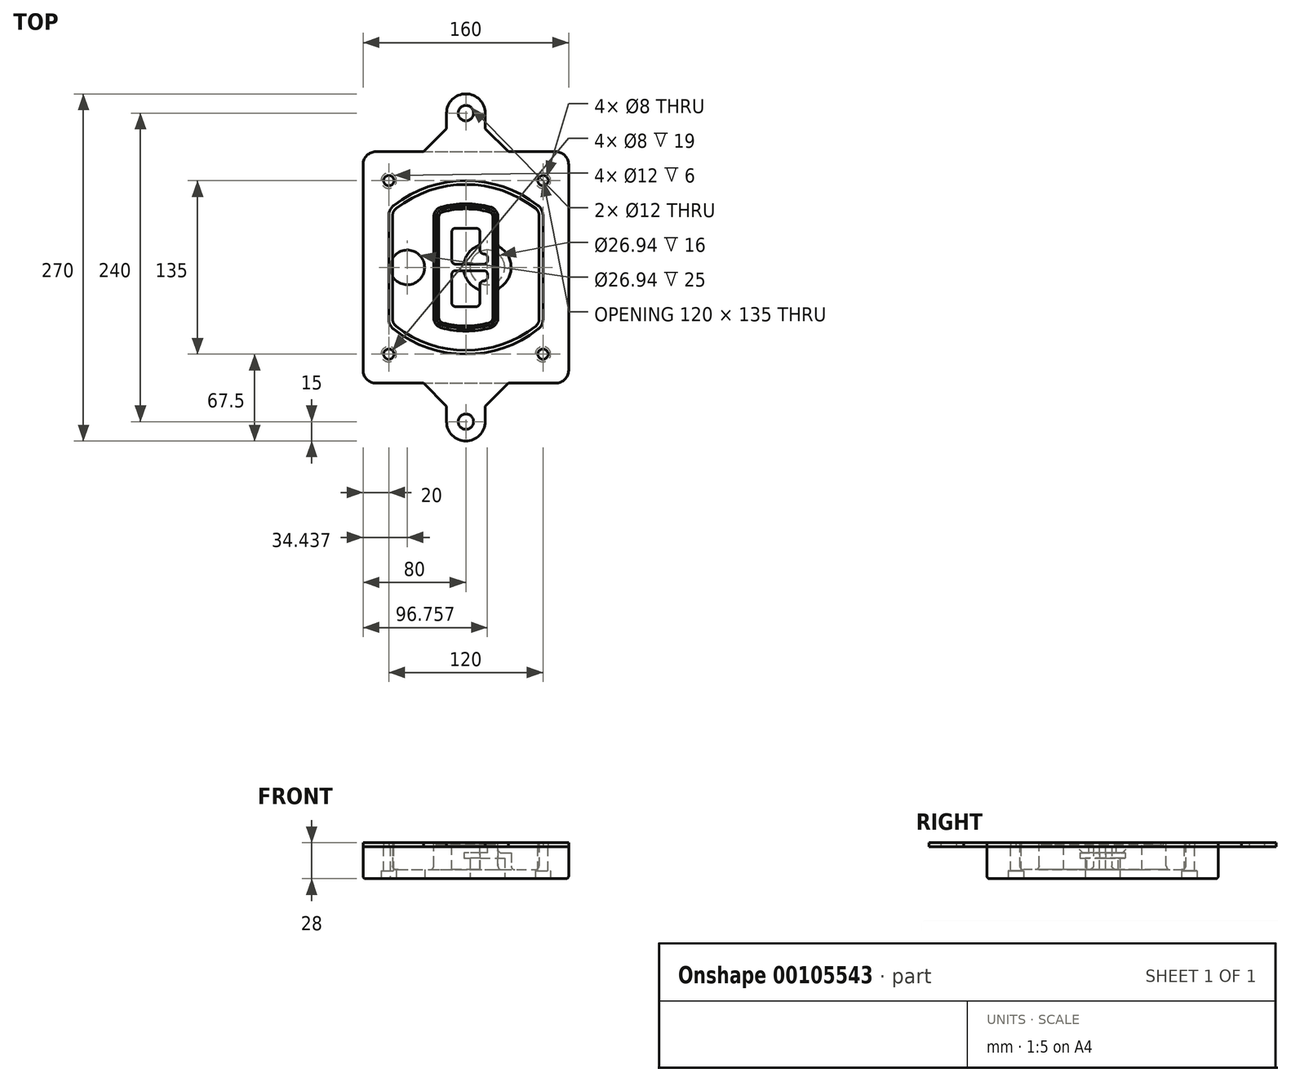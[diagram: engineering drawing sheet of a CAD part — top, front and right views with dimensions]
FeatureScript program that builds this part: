
annotation { "Feature Type Name" : "Feature", "Feature Type Description" : "" }
export const myFeature = defineFeature(function(context is Context, id is Id, definition is map)
    precondition{}
    {
        {
            var Q0;
            Q0=qCreatedBy(makeId("Top.planeOp"),FACE);
            var sketch = newSketch(context, id + "F0", { "sketchPlane" : qUnion([Q0])});
            skPoint(sketch, "E0.rect.middle", {"position": v(0, 0) * mm});
            skLineSegment(sketch, "E1.bottom", {"start": v(-70, -90) * mm, "end": v(70, -90) * mm});
            skLineSegment(sketch, "E1.top", {"start": v(-70, 90) * mm, "end": v(70, 90) * mm});
            skLineSegment(sketch, "E1.left", {"start": v(-80, -80) * mm, "end": v(-80, 80) * mm});
            skLineSegment(sketch, "E1.right", {"start": v(80, -80) * mm, "end": v(80, 80) * mm});
            skLineSegment(sketch, "E2", {"start": v(-80, 90) * mm, "end": v(80, -90) * mm, "construction": true});
            skLineSegment(sketch, "E3", {"start": v(80, 90) * mm, "end": v(-80, -90) * mm, "construction": true});
            skCircle(sketch, "E4", {"center": v(-60, 67.5) * mm, "radius": 4 * mm});
            skCircle(sketch, "E5", {"center": v(60, 67.5) * mm, "radius": 4 * mm});
            skCircle(sketch, "E6", {"center": v(60, -67.5) * mm, "radius": 4 * mm});
            skCircle(sketch, "E7", {"center": v(-60, -67.5) * mm, "radius": 4 * mm});
            skLineSegment(sketch, "E8", {"start": v(-60, 67.5) * mm, "end": v(60, 67.5) * mm, "construction": true});
            skLineSegment(sketch, "E9", {"start": v(60, 67.5) * mm, "end": v(60, -67.5) * mm, "construction": true});
            skLineSegment(sketch, "E10", {"start": v(60, -67.5) * mm, "end": v(-60, -67.5) * mm, "construction": true});
            skLineSegment(sketch, "E11", {"start": v(-60, -67.5) * mm, "end": v(-60, 67.5) * mm, "construction": true});
            skLineSegment(sketch, "E12", {"start": v(-60, 40.3) * mm, "end": v(-60, -40.3) * mm});
            skLineSegment(sketch, "E13", {"start": v(60, 40.3) * mm, "end": v(60, -40.3) * mm});
            skArc(sketch, "E14", {"start": v(56.15, 48.18) * mm, "mid": v(0, 67.5) * mm, "end": v(-56.15, 48.18) * mm});
            skArc(sketch, "E15", {"start": v(-56.15, -48.18) * mm, "mid": v(0, -67.5) * mm, "end": v(56.15, -48.18) * mm});
            skLineSegment(sketch, "E16", {"start": v(-60, 0) * mm, "end": v(60, 0) * mm, "construction": true});
            skPoint(sketch, "E17.visualSharp", {"position": v(-60, -45) * mm});
            skArc(sketch, "E17.filletArc", {"start": v(-60, -40.3) * mm, "mid": v(-58.99, -44.68) * mm, "end": v(-56.15, -48.18) * mm});
            skPoint(sketch, "E18.visualSharp", {"position": v(-60, 45) * mm});
            skArc(sketch, "E18.filletArc", {"start": v(-56.15, 48.18) * mm, "mid": v(-58.99, 44.68) * mm, "end": v(-60, 40.3) * mm});
            skPoint(sketch, "E19.visualSharp", {"position": v(60, 45) * mm});
            skArc(sketch, "E19.filletArc", {"start": v(60, 40.3) * mm, "mid": v(58.99, 44.68) * mm, "end": v(56.15, 48.18) * mm});
            skPoint(sketch, "E20.visualSharp", {"position": v(60, -45) * mm});
            skArc(sketch, "E20.filletArc", {"start": v(56.15, -48.18) * mm, "mid": v(58.99, -44.68) * mm, "end": v(60, -40.3) * mm});
            skPoint(sketch, "E21.visualSharp", {"position": v(-80, 90) * mm});
            skArc(sketch, "E21.filletArc", {"start": v(-70, 90) * mm, "mid": v(-77.07, 87.07) * mm, "end": v(-80, 80) * mm});
            skPoint(sketch, "E22.visualSharp", {"position": v(80, 90) * mm});
            skArc(sketch, "E22.filletArc", {"start": v(80, 80) * mm, "mid": v(77.07, 87.07) * mm, "end": v(70, 90) * mm});
            skPoint(sketch, "E23.visualSharp", {"position": v(80, -90) * mm});
            skArc(sketch, "E23.filletArc", {"start": v(70, -90) * mm, "mid": v(77.07, -87.07) * mm, "end": v(80, -80) * mm});
            skPoint(sketch, "E24.visualSharp", {"position": v(-80, -90) * mm});
            skArc(sketch, "E24.filletArc", {"start": v(-80, -80) * mm, "mid": v(-77.07, -87.07) * mm, "end": v(-70, -90) * mm});
            skArc(sketch, "E25.0", {"start": v(57, 40.3) * mm, "mid": v(56.3, 43.36) * mm, "end": v(54.3, 45.81) * mm});
            skLineSegment(sketch, "E25.1", {"start": v(57, 40.3) * mm, "end": v(57, -40.3) * mm});
            skArc(sketch, "E25.2", {"start": v(54.3, -45.81) * mm, "mid": v(56.3, -43.36) * mm, "end": v(57, -40.3) * mm});
            skArc(sketch, "E25.3", {"start": v(-54.3, -45.81) * mm, "mid": v(0, -64.5) * mm, "end": v(54.3, -45.81) * mm});
            skArc(sketch, "E25.4", {"start": v(-57, -40.3) * mm, "mid": v(-56.3, -43.36) * mm, "end": v(-54.3, -45.81) * mm});
            skArc(sketch, "E25.5", {"start": v(54.3, 45.81) * mm, "mid": v(0, 64.5) * mm, "end": v(-54.3, 45.81) * mm});
            skLineSegment(sketch, "E25.6", {"start": v(-57, 40.3) * mm, "end": v(-57, -40.3) * mm});
            skArc(sketch, "E25.7", {"start": v(-54.3, 45.81) * mm, "mid": v(-56.3, 43.36) * mm, "end": v(-57, 40.3) * mm});
            skArc(sketch, "E26.0", {"start": v(-58.62, 51.33) * mm, "mid": v(-62.58, 46.43) * mm, "end": v(-64, 40.3) * mm});
            skArc(sketch, "E26.1", {"start": v(58.62, 51.33) * mm, "mid": v(0, 71.5) * mm, "end": v(-58.62, 51.33) * mm});
            skArc(sketch, "E26.2", {"start": v(64, 40.3) * mm, "mid": v(62.58, 46.43) * mm, "end": v(58.62, 51.33) * mm});
            skLineSegment(sketch, "E26.3", {"start": v(64, 40.3) * mm, "end": v(64, -40.3) * mm});
            skArc(sketch, "E26.4", {"start": v(58.62, -51.33) * mm, "mid": v(62.58, -46.43) * mm, "end": v(64, -40.3) * mm});
            skLineSegment(sketch, "E26.5", {"start": v(-64, 40.3) * mm, "end": v(-64, -40.3) * mm});
            skArc(sketch, "E26.6", {"start": v(-58.62, -51.33) * mm, "mid": v(0, -71.5) * mm, "end": v(58.62, -51.33) * mm});
            skArc(sketch, "E26.7", {"start": v(-64, -40.3) * mm, "mid": v(-62.58, -46.43) * mm, "end": v(-58.62, -51.33) * mm});
            skSolve(sketch);
        }
        {
            var Q0;
            Q0=makeQuery(id+"F0.imprint","IMPRINT",FACE,{"disambiguationData":[TD([[makeQuery(id+"F0.imprint","IMPRINT",EDGE,{"derivedFrom":sQuery(id+"F0.wireOp",EDGE,"E1.bottom")}),1.0]])]});
            var Q1;
            Q1=makeQuery(id+"F0.imprint","IMPRINT",FACE,{"disambiguationData":[TD([[makeQuery(id+"F0.imprint","IMPRINT",EDGE,{"derivedFrom":sQuery(id+"F0.wireOp",EDGE,"E12")}),1.0]])]});
            var Q2;
            Q2=makeQuery(id+"F0.imprint","IMPRINT",FACE,{"disambiguationData":[TD([[makeQuery(id+"F0.imprint","IMPRINT",EDGE,{"derivedFrom":sQuery(id+"F0.wireOp",EDGE,"E25.0")}),1.0]])]});
            var Q3;
            Q3=makeQuery(id+"F0.imprint","IMPRINT",FACE,{"disambiguationData":[TD([[makeQuery(id+"F0.imprint","IMPRINT",EDGE,{"derivedFrom":sQuery(id+"F0.wireOp",EDGE,"E12")}),-1.0]])]});
            extrude(context, id + "F1", {"entities" : qUnion([Q0, Q1, Q2, Q3]), "oppositeDirection" : true, "depth" : 25 * mm});
        }
        {
            var Q0;
            Q0=makeQuery(id+"F0.imprint","IMPRINT",FACE,{"disambiguationData":[TD([[makeQuery(id+"F0.imprint","IMPRINT",EDGE,{"derivedFrom":sQuery(id+"F0.wireOp",EDGE,"E12")}),1.0]])]});
            extrude(context, id + "F2", {"entities" : qUnion([Q0]), "operationType" : NewBodyOperationType.ADD, "depth" : 3 * mm});
        }
        {
            var Q0;
            Q0=makeQuery(id+"F0.imprint","IMPRINT",FACE,{"disambiguationData":[TD([[makeQuery(id+"F0.imprint","IMPRINT",EDGE,{"derivedFrom":sQuery(id+"F0.wireOp",EDGE,"E25.0")}),1.0]])]});
            extrude(context, id + "F3", {"entities" : qUnion([Q0]), "operationType" : NewBodyOperationType.REMOVE, "oppositeDirection" : true, "depth" : 18 * mm});
        }
        {
            var Q0;
            Q0=makeQuery(id+"F2.opExtrude","CAP_FACE",FACE,{"disambiguationData":[OSD([sQuery(id+"F0.wireOp",EDGE,"E12"),sQuery(id+"F0.wireOp",EDGE,"E13"),sQuery(id+"F0.wireOp",EDGE,"E14"),sQuery(id+"F0.wireOp",EDGE,"E15"),sQuery(id+"F0.wireOp",EDGE,"E17.filletArc"),sQuery(id+"F0.wireOp",EDGE,"E18.filletArc"),sQuery(id+"F0.wireOp",EDGE,"E19.filletArc"),sQuery(id+"F0.wireOp",EDGE,"E20.filletArc"),sQuery(id+"F0.wireOp",EDGE,"E25.0"),sQuery(id+"F0.wireOp",EDGE,"E25.1"),sQuery(id+"F0.wireOp",EDGE,"E25.2"),sQuery(id+"F0.wireOp",EDGE,"E25.3"),sQuery(id+"F0.wireOp",EDGE,"E25.4"),sQuery(id+"F0.wireOp",EDGE,"E25.5"),sQuery(id+"F0.wireOp",EDGE,"E25.6"),sQuery(id+"F0.wireOp",EDGE,"E25.7")])],"isStart":false});
            var sketch = newSketch(context, id + "F4", { "sketchPlane" : qUnion([Q0])});
            skArc(sketch, "E27.0", {"start": v(-19.08, -46.97) * mm, "mid": v(0, -49.5) * mm, "end": v(19.08, -46.97) * mm});
            skArc(sketch, "E28.0", {"start": v(19.08, 46.97) * mm, "mid": v(0, 49.5) * mm, "end": v(-19.08, 46.97) * mm});
            skLineSegment(sketch, "E29", {"start": v(-25, 39.25) * mm, "end": v(-25, -39.25) * mm});
            skLineSegment(sketch, "E30", {"start": v(25, 39.25) * mm, "end": v(25, -39.25) * mm});
            skLineSegment(sketch, "E31", {"start": v(-25, 45.1) * mm, "end": v(25, 45.1) * mm, "construction": true});
            skLineSegment(sketch, "E32", {"start": v(-25, -45.1) * mm, "end": v(25, -45.1) * mm, "construction": true});
            skPoint(sketch, "E33.visualSharp", {"position": v(-25, 45.1) * mm});
            skArc(sketch, "E33.filletArc", {"start": v(-19.08, 46.97) * mm, "mid": v(-23.35, 44.11) * mm, "end": v(-25, 39.25) * mm});
            skPoint(sketch, "E34.visualSharp", {"position": v(25, 45.1) * mm});
            skArc(sketch, "E34.filletArc", {"start": v(25, 39.25) * mm, "mid": v(23.35, 44.11) * mm, "end": v(19.08, 46.97) * mm});
            skPoint(sketch, "E35.visualSharp", {"position": v(25, -45.1) * mm});
            skArc(sketch, "E35.filletArc", {"start": v(19.08, -46.97) * mm, "mid": v(23.35, -44.11) * mm, "end": v(25, -39.25) * mm});
            skPoint(sketch, "E36.visualSharp", {"position": v(-25, -45.1) * mm});
            skArc(sketch, "E36.filletArc", {"start": v(-25, -39.25) * mm, "mid": v(-23.35, -44.11) * mm, "end": v(-19.08, -46.97) * mm});
            skArc(sketch, "E37.0", {"start": v(54.3, 45.81) * mm, "mid": v(0, 64.5) * mm, "end": v(-54.3, 45.81) * mm});
            skArc(sketch, "E37.1", {"start": v(-54.3, 45.81) * mm, "mid": v(-56.3, 43.36) * mm, "end": v(-57, 40.3) * mm});
            skLineSegment(sketch, "E37.2", {"start": v(-57, 40.3) * mm, "end": v(-57, -40.3) * mm});
            skArc(sketch, "E37.3", {"start": v(-57, -40.3) * mm, "mid": v(-56.3, -43.36) * mm, "end": v(-54.3, -45.81) * mm});
            skArc(sketch, "E37.4", {"start": v(-54.3, -45.81) * mm, "mid": v(0, -64.5) * mm, "end": v(54.3, -45.81) * mm});
            skArc(sketch, "E37.5", {"start": v(54.3, -45.81) * mm, "mid": v(56.3, -43.36) * mm, "end": v(57, -40.3) * mm});
            skLineSegment(sketch, "E37.6", {"start": v(57, 40.3) * mm, "end": v(57, -40.3) * mm});
            skArc(sketch, "E37.7", {"start": v(57, 40.3) * mm, "mid": v(56.3, 43.36) * mm, "end": v(54.3, 45.81) * mm});
            skLineSegment(sketch, "E38.0", {"start": v(23, 39.25) * mm, "end": v(23, -39.25) * mm});
            skArc(sketch, "E38.1", {"start": v(18.56, -45.04) * mm, "mid": v(21.76, -42.9) * mm, "end": v(23, -39.25) * mm});
            skArc(sketch, "E38.2", {"start": v(-18.56, -45.04) * mm, "mid": v(0, -47.5) * mm, "end": v(18.56, -45.04) * mm});
            skArc(sketch, "E38.3", {"start": v(-23, -39.25) * mm, "mid": v(-21.76, -42.9) * mm, "end": v(-18.56, -45.04) * mm});
            skLineSegment(sketch, "E38.4", {"start": v(-23, 39.25) * mm, "end": v(-23, -39.25) * mm});
            skArc(sketch, "E38.5", {"start": v(23, 39.25) * mm, "mid": v(21.76, 42.9) * mm, "end": v(18.56, 45.04) * mm});
            skArc(sketch, "E38.6", {"start": v(-18.56, 45.04) * mm, "mid": v(-21.76, 42.9) * mm, "end": v(-23, 39.25) * mm});
            skArc(sketch, "E38.7", {"start": v(18.56, 45.04) * mm, "mid": v(0, 47.5) * mm, "end": v(-18.56, 45.04) * mm});
            skArc(sketch, "E39.0", {"start": v(21, 39.25) * mm, "mid": v(20.18, 41.68) * mm, "end": v(18.04, 43.1) * mm});
            skLineSegment(sketch, "E39.1", {"start": v(21, 39.25) * mm, "end": v(21, -39.25) * mm});
            skArc(sketch, "E39.2", {"start": v(18.04, -43.1) * mm, "mid": v(20.18, -41.68) * mm, "end": v(21, -39.25) * mm});
            skArc(sketch, "E39.3", {"start": v(-18.04, -43.1) * mm, "mid": v(0, -45.5) * mm, "end": v(18.04, -43.1) * mm});
            skArc(sketch, "E39.4", {"start": v(-21, -39.25) * mm, "mid": v(-20.18, -41.68) * mm, "end": v(-18.04, -43.1) * mm});
            skArc(sketch, "E39.5", {"start": v(18.04, 43.1) * mm, "mid": v(0, 45.5) * mm, "end": v(-18.04, 43.1) * mm});
            skLineSegment(sketch, "E39.6", {"start": v(-21, 39.25) * mm, "end": v(-21, -39.25) * mm});
            skArc(sketch, "E39.7", {"start": v(-18.04, 43.1) * mm, "mid": v(-20.18, 41.68) * mm, "end": v(-21, 39.25) * mm});
            skLineSegment(sketch, "E40", {"start": v(-25, 0) * mm, "end": v(25, 0) * mm, "construction": true});
            skLineSegment(sketch, "E41", {"start": v(-11, 5.5) * mm, "end": v(-11, 27.5) * mm});
            skLineSegment(sketch, "E42", {"start": v(-8, 30.5) * mm, "end": v(8, 30.5) * mm});
            skLineSegment(sketch, "E43", {"start": v(11, 27.5) * mm, "end": v(11, 13.5) * mm});
            skLineSegment(sketch, "E44", {"start": v(14, 10.5) * mm, "end": v(14, 10.5) * mm});
            skLineSegment(sketch, "E45", {"start": v(17, 7.5) * mm, "end": v(17, 5.5) * mm});
            skLineSegment(sketch, "E46", {"start": v(14, 2.5) * mm, "end": v(-8, 2.5) * mm});
            skPoint(sketch, "E47.visualSharp", {"position": v(-11, 30.5) * mm});
            skArc(sketch, "E47.filletArc", {"start": v(-8, 30.5) * mm, "mid": v(-10.12, 29.62) * mm, "end": v(-11, 27.5) * mm});
            skPoint(sketch, "E48.visualSharp", {"position": v(11, 30.5) * mm});
            skArc(sketch, "E48.filletArc", {"start": v(11, 27.5) * mm, "mid": v(10.12, 29.62) * mm, "end": v(8, 30.5) * mm});
            skPoint(sketch, "E49.visualSharp", {"position": v(11, 10.5) * mm});
            skArc(sketch, "E49.filletArc", {"start": v(11, 13.5) * mm, "mid": v(11.88, 11.38) * mm, "end": v(14, 10.5) * mm});
            skPoint(sketch, "E50.visualSharp", {"position": v(17, 10.5) * mm});
            skArc(sketch, "E50.filletArc", {"start": v(17, 7.5) * mm, "mid": v(16.12, 9.62) * mm, "end": v(14, 10.5) * mm});
            skPoint(sketch, "E51.visualSharp", {"position": v(17, 2.5) * mm});
            skArc(sketch, "E51.filletArc", {"start": v(14, 2.5) * mm, "mid": v(16.12, 3.38) * mm, "end": v(17, 5.5) * mm});
            skPoint(sketch, "E52.visualSharp", {"position": v(-11, 2.5) * mm});
            skArc(sketch, "E52.filletArc", {"start": v(-11, 5.5) * mm, "mid": v(-10.12, 3.38) * mm, "end": v(-8, 2.5) * mm});
            skLineSegment(sketch, "E53.0.MirrorCS", {"start": v(14, -2.5) * mm, "end": v(-8, -2.5) * mm});
            skArc(sketch, "E54.0.MirrorCS", {"start": v(-11, -5.5) * mm, "mid": v(-10.12, -3.38) * mm, "end": v(-8, -2.5) * mm});
            skLineSegment(sketch, "E55.0.MirrorCS", {"start": v(-11, -5.5) * mm, "end": v(-11, -27.5) * mm});
            skArc(sketch, "E56.0.MirrorCS", {"start": v(-8, -30.5) * mm, "mid": v(-10.12, -29.62) * mm, "end": v(-11, -27.5) * mm});
            skLineSegment(sketch, "E57.0.MirrorCS", {"start": v(-8, -30.5) * mm, "end": v(8, -30.5) * mm});
            skArc(sketch, "E58.0.MirrorCS", {"start": v(11, -27.5) * mm, "mid": v(10.12, -29.62) * mm, "end": v(8, -30.5) * mm});
            skLineSegment(sketch, "E59.0.MirrorCS", {"start": v(11, -27.5) * mm, "end": v(11, -13.5) * mm});
            skArc(sketch, "E60.0.MirrorCS", {"start": v(11, -13.5) * mm, "mid": v(11.88, -11.38) * mm, "end": v(14, -10.5) * mm});
            skArc(sketch, "E61.0.MirrorCS", {"start": v(17, -7.5) * mm, "mid": v(16.12, -9.62) * mm, "end": v(14, -10.5) * mm});
            skLineSegment(sketch, "E62.0.MirrorCS", {"start": v(17, -7.5) * mm, "end": v(17, -5.5) * mm});
            skArc(sketch, "E63.0.MirrorCS", {"start": v(14, -2.5) * mm, "mid": v(16.12, -3.38) * mm, "end": v(17, -5.5) * mm});
            skSolve(sketch);
        }
        {
            var Q0;
            Q0=makeQuery(id+"F4.imprint","IMPRINT",FACE,{"disambiguationData":[TD([[makeQuery(id+"F4.imprint","IMPRINT",EDGE,{"derivedFrom":sQuery(id+"F4.wireOp",EDGE,"E27.0")}),1.0]])]});
            var Q1;
            Q1=makeQuery(id+"F4.imprint","IMPRINT",FACE,{"disambiguationData":[TD([[makeQuery(id+"F4.imprint","IMPRINT",EDGE,{"derivedFrom":sQuery(id+"F4.wireOp",EDGE,"E38.0")}),-1.0]])]});
            var Q2;
            Q2=makeQuery(id+"F4.imprint","IMPRINT",FACE,{"disambiguationData":[TD([[makeQuery(id+"F4.imprint","IMPRINT",EDGE,{"derivedFrom":sQuery(id+"F4.wireOp",EDGE,"E39.0")}),1.0]])]});
            extrude(context, id + "F5", {"entities" : qUnion([Q0, Q1, Q2]), "operationType" : NewBodyOperationType.ADD, "endBound" : BoundingType.UP_TO_NEXT, "oppositeDirection" : true, "depth" : 25 * mm});
        }
        {
            var Q0;
            Q0=makeQuery(id+"F4.imprint","IMPRINT",FACE,{"disambiguationData":[TD([[makeQuery(id+"F4.imprint","IMPRINT",EDGE,{"derivedFrom":sQuery(id+"F4.wireOp",EDGE,"E38.0")}),-1.0]])]});
            extrude(context, id + "F6", {"entities" : qUnion([Q0]), "operationType" : NewBodyOperationType.REMOVE, "oppositeDirection" : true, "depth" : 2 * mm});
        }
        {
            var Q0;
            Q0=makeQuery(id+"F1.opExtrude","CAP_FACE",FACE,{"disambiguationData":[OSD([sQuery(id+"F0.wireOp",EDGE,"E1.bottom"),sQuery(id+"F0.wireOp",EDGE,"E1.top"),sQuery(id+"F0.wireOp",EDGE,"E1.left"),sQuery(id+"F0.wireOp",EDGE,"E1.right"),sQuery(id+"F0.wireOp",EDGE,"E4"),sQuery(id+"F0.wireOp",EDGE,"E5"),sQuery(id+"F0.wireOp",EDGE,"E6"),sQuery(id+"F0.wireOp",EDGE,"E7"),sQuery(id+"F0.wireOp",EDGE,"E21.filletArc"),sQuery(id+"F0.wireOp",EDGE,"E22.filletArc"),sQuery(id+"F0.wireOp",EDGE,"E23.filletArc"),sQuery(id+"F0.wireOp",EDGE,"E24.filletArc")])],"isStart":false});
            var sketch = newSketch(context, id + "F7", { "sketchPlane" : qUnion([Q0])});
            skCircle(sketch, "E64", {"center": v(16.76, 0) * mm, "radius": 13.47 * mm});
            skCircle(sketch, "E65", {"center": v(-45.56, 0) * mm, "radius": 13.47 * mm});
            skLineSegment(sketch, "E66", {"start": v(80, 0) * mm, "end": v(-80, 0) * mm});
            skCircle(sketch, "E67", {"center": v(16.76, 0) * mm, "radius": 18.47 * mm});
            skCircle(sketch, "E68", {"center": v(60, -67.5) * mm, "radius": 6 * mm});
            skCircle(sketch, "E69", {"center": v(-60, -67.5) * mm, "radius": 6 * mm});
            skCircle(sketch, "E70", {"center": v(-60, 67.5) * mm, "radius": 6 * mm});
            skCircle(sketch, "E71", {"center": v(60, 67.5) * mm, "radius": 6 * mm});
            skSolve(sketch);
        }
        {
            var Q0;
            {var subQ1=sQuery(id+"F7.wireOp",EDGE,"E66");var subQ4=sQuery(id+"F7.wireOp",EDGE,"E64");var subQ6=makeQuery(id+"F7.imprint","INTERSECT",VERTEX,{"disambiguationData":[OD(0.0)],"derivedFrom":[subQ4,subQ1]});Q0=makeQuery(id+"F7.imprint","IMPRINT",FACE,{"disambiguationData":[TD([[makeQuery(id+"F7.imprint","IMPRINT",EDGE,{"disambiguationData":[TD([[subQ6,-1.0]])],"derivedFrom":subQ4}),-1.0]])]});}
            var Q1;
            {var subQ0=sQuery(id+"F7.wireOp",EDGE,"E66");var subQ1=sQuery(id+"F7.wireOp",EDGE,"E64");var subQ3=makeQuery(id+"F7.imprint","INTERSECT",VERTEX,{"disambiguationData":[OD(0.0)],"derivedFrom":[subQ1,subQ0]});Q1=makeQuery(id+"F7.imprint","IMPRINT",FACE,{"disambiguationData":[TD([[makeQuery(id+"F7.imprint","IMPRINT",EDGE,{"disambiguationData":[TD([[subQ3,-1.0]])],"derivedFrom":subQ1}),1.0]])]});}
            var Q2;
            {var subQ0=sQuery(id+"F7.wireOp",EDGE,"E66");var subQ1=sQuery(id+"F7.wireOp",EDGE,"E64");var subQ3=makeQuery(id+"F7.imprint","INTERSECT",VERTEX,{"disambiguationData":[OD(0.0)],"derivedFrom":[subQ1,subQ0]});Q2=makeQuery(id+"F7.imprint","IMPRINT",FACE,{"disambiguationData":[TD([[makeQuery(id+"F7.imprint","IMPRINT",EDGE,{"disambiguationData":[TD([[subQ3,1.0]])],"derivedFrom":subQ1}),1.0]])]});}
            var Q3;
            {var subQ1=sQuery(id+"F7.wireOp",EDGE,"E66");var subQ4=sQuery(id+"F7.wireOp",EDGE,"E64");var subQ6=makeQuery(id+"F7.imprint","INTERSECT",VERTEX,{"disambiguationData":[OD(0.0)],"derivedFrom":[subQ4,subQ1]});Q3=makeQuery(id+"F7.imprint","IMPRINT",FACE,{"disambiguationData":[TD([[makeQuery(id+"F7.imprint","IMPRINT",EDGE,{"disambiguationData":[TD([[subQ6,1.0]])],"derivedFrom":subQ4}),-1.0]])]});}
            extrude(context, id + "F8", {"entities" : qUnion([Q0, Q1, Q2, Q3]), "operationType" : NewBodyOperationType.ADD, "oppositeDirection" : true, "depth" : 20 * mm});
        }
        {
            var Q0;
            {var subQ0=sQuery(id+"F7.wireOp",EDGE,"E66");var subQ1=sQuery(id+"F7.wireOp",EDGE,"E64");var subQ3=makeQuery(id+"F7.imprint","INTERSECT",VERTEX,{"disambiguationData":[OD(0.0)],"derivedFrom":[subQ1,subQ0]});Q0=makeQuery(id+"F7.imprint","IMPRINT",FACE,{"disambiguationData":[TD([[makeQuery(id+"F7.imprint","IMPRINT",EDGE,{"disambiguationData":[TD([[subQ3,-1.0]])],"derivedFrom":subQ1}),1.0]])]});}
            var Q1;
            {var subQ0=sQuery(id+"F7.wireOp",EDGE,"E66");var subQ1=sQuery(id+"F7.wireOp",EDGE,"E64");var subQ3=makeQuery(id+"F7.imprint","INTERSECT",VERTEX,{"disambiguationData":[OD(0.0)],"derivedFrom":[subQ1,subQ0]});Q1=makeQuery(id+"F7.imprint","IMPRINT",FACE,{"disambiguationData":[TD([[makeQuery(id+"F7.imprint","IMPRINT",EDGE,{"disambiguationData":[TD([[subQ3,1.0]])],"derivedFrom":subQ1}),1.0]])]});}
            extrude(context, id + "F9", {"entities" : qUnion([Q0, Q1]), "operationType" : NewBodyOperationType.REMOVE, "oppositeDirection" : true, "depth" : 16 * mm});
        }
        {
            var Q0;
            {var subQ0=sQuery(id+"F7.wireOp",EDGE,"E66");var subQ1=sQuery(id+"F7.wireOp",EDGE,"E65");var subQ3=makeQuery(id+"F7.imprint","INTERSECT",VERTEX,{"disambiguationData":[OD(0.0)],"derivedFrom":[subQ1,subQ0]});Q0=makeQuery(id+"F7.imprint","IMPRINT",FACE,{"disambiguationData":[TD([[makeQuery(id+"F7.imprint","IMPRINT",EDGE,{"disambiguationData":[TD([[subQ3,-1.0]])],"derivedFrom":subQ1}),1.0]])]});}
            var Q1;
            {var subQ0=sQuery(id+"F7.wireOp",EDGE,"E66");var subQ1=sQuery(id+"F7.wireOp",EDGE,"E65");var subQ3=makeQuery(id+"F7.imprint","INTERSECT",VERTEX,{"disambiguationData":[OD(0.0)],"derivedFrom":[subQ1,subQ0]});Q1=makeQuery(id+"F7.imprint","IMPRINT",FACE,{"disambiguationData":[TD([[makeQuery(id+"F7.imprint","IMPRINT",EDGE,{"disambiguationData":[TD([[subQ3,1.0]])],"derivedFrom":subQ1}),1.0]])]});}
            extrude(context, id + "F10", {"entities" : qUnion([Q0, Q1]), "operationType" : NewBodyOperationType.REMOVE, "oppositeDirection" : true, "depth" : 25 * mm});
        }
        {
            var Q0;
            Q0=makeQuery(id+"F7.imprint","IMPRINT",FACE,{"disambiguationData":[TD([[makeQuery(id+"F7.imprint","IMPRINT",EDGE,{"derivedFrom":sQuery(id+"F7.wireOp",EDGE,"E68")}),1.0]])]});
            var Q1;
            Q1=makeQuery(id+"F7.imprint","IMPRINT",FACE,{"disambiguationData":[TD([[makeQuery(id+"F7.imprint","IMPRINT",EDGE,{"derivedFrom":makeQuery(id+"F1.opExtrude","CAP_EDGE",EDGE,{"disambiguationData":[OSD([sQuery(id+"F0.wireOp",EDGE,"E5")])],"isStart":false})}),-1.0]])]});
            var Q2;
            Q2=makeQuery(id+"F7.imprint","IMPRINT",FACE,{"disambiguationData":[TD([[makeQuery(id+"F7.imprint","IMPRINT",EDGE,{"derivedFrom":sQuery(id+"F7.wireOp",EDGE,"E69")}),1.0]])]});
            var Q3;
            Q3=makeQuery(id+"F7.imprint","IMPRINT",FACE,{"disambiguationData":[TD([[makeQuery(id+"F7.imprint","IMPRINT",EDGE,{"derivedFrom":makeQuery(id+"F1.opExtrude","CAP_EDGE",EDGE,{"disambiguationData":[OSD([sQuery(id+"F0.wireOp",EDGE,"E4")])],"isStart":false})}),-1.0]])]});
            var Q4;
            Q4=makeQuery(id+"F7.imprint","IMPRINT",FACE,{"disambiguationData":[TD([[makeQuery(id+"F7.imprint","IMPRINT",EDGE,{"derivedFrom":sQuery(id+"F7.wireOp",EDGE,"E70")}),1.0]])]});
            var Q5;
            Q5=makeQuery(id+"F7.imprint","IMPRINT",FACE,{"disambiguationData":[TD([[makeQuery(id+"F7.imprint","IMPRINT",EDGE,{"derivedFrom":makeQuery(id+"F1.opExtrude","CAP_EDGE",EDGE,{"disambiguationData":[OSD([sQuery(id+"F0.wireOp",EDGE,"E7")])],"isStart":false})}),-1.0]])]});
            var Q6;
            Q6=makeQuery(id+"F7.imprint","IMPRINT",FACE,{"disambiguationData":[TD([[makeQuery(id+"F7.imprint","IMPRINT",EDGE,{"derivedFrom":sQuery(id+"F7.wireOp",EDGE,"E71")}),1.0]])]});
            var Q7;
            Q7=makeQuery(id+"F7.imprint","IMPRINT",FACE,{"disambiguationData":[TD([[makeQuery(id+"F7.imprint","IMPRINT",EDGE,{"derivedFrom":makeQuery(id+"F1.opExtrude","CAP_EDGE",EDGE,{"disambiguationData":[OSD([sQuery(id+"F0.wireOp",EDGE,"E6")])],"isStart":false})}),-1.0]])]});
            extrude(context, id + "F11", {"entities" : qUnion([Q0, Q1, Q2, Q3, Q4, Q5, Q6, Q7]), "operationType" : NewBodyOperationType.REMOVE, "oppositeDirection" : true, "depth" : 6 * mm});
        }
        {
            var Q0;
            Q0=makeQuery(id+"F9.boolean.opBoolean","COPY",FACE,{"derivedFrom":makeQuery(id+"F9.opExtrude","CAP_FACE",FACE,{"disambiguationData":[OSD([sQuery(id+"F7.wireOp",EDGE,"E64")])],"isStart":false})});
            var sketch = newSketch(context, id + "F12", { "sketchPlane" : qUnion([Q0])});
            skArc(sketch, "E72.0", {"start": v(11, 17.55) * mm, "mid": v(2.57, 11.82) * mm, "end": v(-1.54, 2.5) * mm});
            skArc(sketch, "E72.1", {"start": v(-1.54, -2.5) * mm, "mid": v(2.57, -11.82) * mm, "end": v(11, -17.55) * mm});
            skLineSegment(sketch, "E73", {"start": v(-1.54, -2.5) * mm, "end": v(14, -2.5) * mm});
            skLineSegment(sketch, "E74.0", {"start": v(14, 2.5) * mm, "end": v(-1.54, 2.5) * mm});
            skArc(sketch, "E74.1", {"start": v(14, 2.5) * mm, "mid": v(16.12, 3.38) * mm, "end": v(17, 5.5) * mm});
            skLineSegment(sketch, "E74.2", {"start": v(17, 7.5) * mm, "end": v(17, 5.5) * mm});
            skArc(sketch, "E74.3", {"start": v(17, 7.5) * mm, "mid": v(16.12, 9.62) * mm, "end": v(14, 10.5) * mm});
            skArc(sketch, "E74.4", {"start": v(11, 13.5) * mm, "mid": v(11.88, 11.38) * mm, "end": v(14, 10.5) * mm});
            skLineSegment(sketch, "E74.5", {"start": v(11, 17.55) * mm, "end": v(11, 13.5) * mm});
            skLineSegment(sketch, "E74.7", {"start": v(14, -2.5) * mm, "end": v(-1.54, -2.5) * mm});
            skArc(sketch, "E74.8", {"start": v(14, -2.5) * mm, "mid": v(16.12, -3.38) * mm, "end": v(17, -5.5) * mm});
            skLineSegment(sketch, "E74.9", {"start": v(17, -7.5) * mm, "end": v(17, -5.5) * mm});
            skArc(sketch, "E74.10", {"start": v(17, -7.5) * mm, "mid": v(16.12, -9.62) * mm, "end": v(14, -10.5) * mm});
            skArc(sketch, "E74.11", {"start": v(11, -13.5) * mm, "mid": v(11.88, -11.38) * mm, "end": v(14, -10.5) * mm});
            skLineSegment(sketch, "E74.12", {"start": v(11, -17.55) * mm, "end": v(11, -13.5) * mm});
            skPoint(sketch, "E75.orphan", {"position": v(11, -27.5) * mm});
            skPoint(sketch, "E76.orphan", {"position": v(-8, -2.5) * mm});
            skPoint(sketch, "E77.orphan", {"position": v(-8, 2.5) * mm});
            skPoint(sketch, "E78.orphan", {"position": v(11, 27.5) * mm});
            skSolve(sketch);
        }
        {
            var Q0;
            {var subQ7=sQuery(id+"F12.wireOp",EDGE,"E72.0");var subQ14=sQuery(id+"F12.wireOp",EDGE,"E72.1");var subQ16=sQuery(id+"F12.wireOp",EDGE,"E74.1");var subQ18=sQuery(id+"F12.wireOp",EDGE,"E74.8");Q0=qUnion([makeQuery(id+"F12.imprint","IMPRINT",FACE,{"disambiguationData":[TD([[makeQuery(id+"F12.imprint","IMPRINT",EDGE,{"derivedFrom":subQ7}),1.0]])]}),makeQuery(id+"F12.imprint","IMPRINT",FACE,{"disambiguationData":[TD([[makeQuery(id+"F12.imprint","IMPRINT",EDGE,{"derivedFrom":subQ14}),1.0]])]}),makeQuery(id+"F12.imprint","IMPRINT",FACE,{"disambiguationData":[TD([[makeQuery(id+"F12.imprint","IMPRINT",EDGE,{"derivedFrom":subQ16}),1.0]])]}),makeQuery(id+"F12.imprint","IMPRINT",FACE,{"disambiguationData":[TD([[makeQuery(id+"F12.imprint","IMPRINT",EDGE,{"derivedFrom":subQ18}),-1.0]])]})]);}
            var Q1;
            Q1=makeQuery(id+"F5.boolean.opBoolean","SPLIT",FACE,{"disambiguationData":[TD([makeQuery(id+"F5.opExtrude","SWEPT_FACE",FACE,{"disambiguationData":[OSD([sQuery(id+"F4.wireOp",EDGE,"E41")])]})])],"derivedFrom":makeQuery(id+"F3.boolean.opBoolean","COPY",FACE,{"derivedFrom":makeQuery(id+"F3.opExtrude","CAP_FACE",FACE,{"disambiguationData":[OSD([sQuery(id+"F0.wireOp",EDGE,"E25.0"),sQuery(id+"F0.wireOp",EDGE,"E25.1"),sQuery(id+"F0.wireOp",EDGE,"E25.2"),sQuery(id+"F0.wireOp",EDGE,"E25.3"),sQuery(id+"F0.wireOp",EDGE,"E25.4"),sQuery(id+"F0.wireOp",EDGE,"E25.5"),sQuery(id+"F0.wireOp",EDGE,"E25.6"),sQuery(id+"F0.wireOp",EDGE,"E25.7")])],"isStart":false})})});
            extrude(context, id + "F13", {"entities" : qUnion([Q0]), "operationType" : NewBodyOperationType.REMOVE, "endBound" : BoundingType.UP_TO_SURFACE, "endBoundEntityFace" : qUnion([Q1]), "depth" : 25 * mm});
        }
        {
            var Q0;
            Q0=makeQuery(id+"F3.boolean.opBoolean","COPY",EDGE,{"derivedFrom":makeQuery(id+"F3.opExtrude","CAP_EDGE",EDGE,{"disambiguationData":[OSD([sQuery(id+"F0.wireOp",EDGE,"E25.6")])],"isStart":false})});
            var Q1;
            Q1=makeQuery(id+"F8.boolean.opBoolean","INTERSECT",EDGE,{"derivedFrom":[makeQuery(id+"F5.opExtrude","SWEPT_FACE",FACE,{"disambiguationData":[OSD([sQuery(id+"F4.wireOp",EDGE,"E30")])]}),makeQuery(id+"F8.opExtrude","CAP_FACE",FACE,{"disambiguationData":[OSD([sQuery(id+"F7.wireOp",EDGE,"E67")])],"isStart":false})]});
            var Q2;
            Q2=makeQuery(id+"F8.boolean.opBoolean","INTERSECT",EDGE,{"disambiguationData":[OD(1.0)],"derivedFrom":[makeQuery(id+"F5.opExtrude","SWEPT_FACE",FACE,{"disambiguationData":[OSD([sQuery(id+"F4.wireOp",EDGE,"E30")])]}),makeQuery(id+"F8.opExtrude","SWEPT_FACE",FACE,{"disambiguationData":[OSD([sQuery(id+"F7.wireOp",EDGE,"E67")])]})]});
            var Q3;
            {var subQ0=sQuery(id+"F4.wireOp",EDGE,"E30");Q3=makeQuery(id+"F8.boolean.opBoolean","SPLIT",EDGE,{"disambiguationData":[TD([makeQuery(id+"F5.opExtrude","SWEPT_FACE",FACE,{"disambiguationData":[OSD([sQuery(id+"F4.wireOp",EDGE,"E35.filletArc")])]})])],"derivedFrom":makeQuery(id+"F5.opExtrude","CAP_EDGE",EDGE,{"disambiguationData":[OSD([subQ0])],"isStart":false})});}
            var Q4;
            {var subQ0=sQuery(id+"F0.wireOp",EDGE,"E25.7");var subQ1=sQuery(id+"F0.wireOp",EDGE,"E25.1");var subQ2=sQuery(id+"F0.wireOp",EDGE,"E25.6");var subQ3=sQuery(id+"F0.wireOp",EDGE,"E25.5");var subQ4=sQuery(id+"F0.wireOp",EDGE,"E25.4");var subQ5=sQuery(id+"F0.wireOp",EDGE,"E25.0");var subQ6=sQuery(id+"F0.wireOp",EDGE,"E25.2");var subQ7=sQuery(id+"F0.wireOp",EDGE,"E25.3");Q4=makeQuery(id+"F8.boolean.opBoolean","INTERSECT",EDGE,{"derivedFrom":[makeQuery(id+"F5.boolean.opBoolean","SPLIT",FACE,{"disambiguationData":[TD([makeQuery(id+"F2.opExtrude","SWEPT_FACE",FACE,{"disambiguationData":[OSD([subQ5])]})])],"derivedFrom":makeQuery(id+"F3.boolean.opBoolean","COPY",FACE,{"derivedFrom":makeQuery(id+"F3.opExtrude","CAP_FACE",FACE,{"disambiguationData":[OSD([subQ5,subQ1,subQ6,subQ7,subQ4,subQ3,subQ2,subQ0])],"isStart":false})})}),makeQuery(id+"F8.opExtrude","SWEPT_FACE",FACE,{"disambiguationData":[OSD([sQuery(id+"F7.wireOp",EDGE,"E67")])]})]});}
            var Q5;
            Q5=makeQuery(id+"F8.boolean.opBoolean","INTERSECT",EDGE,{"disambiguationData":[OD(0.0)],"derivedFrom":[makeQuery(id+"F5.opExtrude","SWEPT_FACE",FACE,{"disambiguationData":[OSD([sQuery(id+"F4.wireOp",EDGE,"E30")])]}),makeQuery(id+"F8.opExtrude","SWEPT_FACE",FACE,{"disambiguationData":[OSD([sQuery(id+"F7.wireOp",EDGE,"E67")])]})]});
            fillet(context, id + "F14", {"entities" : qUnion([Q0, Q1, Q2, Q3, Q4, Q5]), "radius" : 3 * mm, "tangentPropagation" : true, "allowEdgeOverflow" : false});
        }
        {
            var Q0;
            Q0=makeQuery(id+"F1.opExtrude","CAP_EDGE",EDGE,{"disambiguationData":[OSD([sQuery(id+"F0.wireOp",EDGE,"E1.bottom")])],"isStart":false});
            fillet(context, id + "F15", {"entities" : qUnion([Q0]), "radius" : 2 * mm, "tangentPropagation" : true, "allowEdgeOverflow" : false});
        }
        {
            var Q0;
            {var subQ0=sQuery(id+"F0.wireOp",EDGE,"E22.filletArc");var subQ1=sQuery(id+"F0.wireOp",EDGE,"E7");var subQ2=sQuery(id+"F0.wireOp",EDGE,"E6");var subQ3=sQuery(id+"F0.wireOp",EDGE,"E5");var subQ4=sQuery(id+"F0.wireOp",EDGE,"E4");var subQ5=sQuery(id+"F0.wireOp",EDGE,"E1.bottom");var subQ6=sQuery(id+"F0.wireOp",EDGE,"E21.filletArc");var subQ7=sQuery(id+"F0.wireOp",EDGE,"E1.top");var subQ8=sQuery(id+"F0.wireOp",EDGE,"E1.left");var subQ9=sQuery(id+"F0.wireOp",EDGE,"E1.right");var subQ10=sQuery(id+"F0.wireOp",EDGE,"E23.filletArc");var subQ11=sQuery(id+"F0.wireOp",EDGE,"E24.filletArc");Q0=makeQuery(id+"F2.boolean.opBoolean","SPLIT",FACE,{"disambiguationData":[TD([makeQuery(id+"F1.opExtrude","SWEPT_FACE",FACE,{"disambiguationData":[OSD([subQ5])]})])],"derivedFrom":makeQuery(id+"F1.opExtrude","CAP_FACE",FACE,{"disambiguationData":[OSD([subQ5,subQ7,subQ8,subQ9,subQ4,subQ3,subQ2,subQ1,subQ6,subQ0,subQ10,subQ11])],"isStart":true})});}
            var sketch = newSketch(context, id + "F16", { "sketchPlane" : qUnion([Q0])});
            skArc(sketch, "E79.0", {"start": v(56.15, 48.18) * mm, "mid": v(0, 67.5) * mm, "end": v(-56.15, 48.18) * mm});
            skLineSegment(sketch, "E80.0", {"start": v(60, 40.3) * mm, "end": v(60, -40.3) * mm});
            skLineSegment(sketch, "E81.0", {"start": v(-60, 40.3) * mm, "end": v(-60, -40.3) * mm});
            skCircle(sketch, "E82.0", {"center": v(-60, -67.5) * mm, "radius": 4 * mm});
            skCircle(sketch, "E83.0", {"center": v(60, -67.5) * mm, "radius": 4 * mm});
            skCircle(sketch, "E84.0", {"center": v(60, 67.5) * mm, "radius": 4 * mm});
            skCircle(sketch, "E85.0", {"center": v(-60, 67.5) * mm, "radius": 4 * mm});
            skLineSegment(sketch, "E86.0", {"start": v(-70, 90) * mm, "end": v(70, 90) * mm});
            skLineSegment(sketch, "E87.0", {"start": v(-80, -80) * mm, "end": v(-80, 80) * mm});
            skLineSegment(sketch, "E88.0", {"start": v(80, -80) * mm, "end": v(80, 80) * mm});
            skArc(sketch, "E89.0", {"start": v(-70, 90) * mm, "mid": v(-77.07, 87.07) * mm, "end": v(-80, 80) * mm});
            skArc(sketch, "E90.0", {"start": v(80, 80) * mm, "mid": v(77.07, 87.07) * mm, "end": v(70, 90) * mm});
            skArc(sketch, "E91.0", {"start": v(70, -90) * mm, "mid": v(77.07, -87.07) * mm, "end": v(80, -80) * mm});
            skArc(sketch, "E92.0", {"start": v(-80, -80) * mm, "mid": v(-77.07, -87.07) * mm, "end": v(-70, -90) * mm});
            skArc(sketch, "E93.0", {"start": v(-56.15, -48.18) * mm, "mid": v(0, -67.5) * mm, "end": v(56.15, -48.18) * mm});
            skArc(sketch, "E94.0", {"start": v(-56.15, 48.18) * mm, "mid": v(-58.99, 44.68) * mm, "end": v(-60, 40.3) * mm});
            skArc(sketch, "E95.0", {"start": v(60, 40.3) * mm, "mid": v(58.99, 44.68) * mm, "end": v(56.15, 48.18) * mm});
            skArc(sketch, "E96.0", {"start": v(56.15, -48.18) * mm, "mid": v(58.99, -44.68) * mm, "end": v(60, -40.3) * mm});
            skArc(sketch, "E97.0", {"start": v(-60, -40.3) * mm, "mid": v(-58.99, -44.68) * mm, "end": v(-56.15, -48.18) * mm});
            skLineSegment(sketch, "E98", {"start": v(-33, -90) * mm, "end": v(-15, -108) * mm});
            skLineSegment(sketch, "E99", {"start": v(-15, -108) * mm, "end": v(-15, -120) * mm});
            skLineSegment(sketch, "E100", {"start": v(33, -90) * mm, "end": v(15, -108) * mm});
            skLineSegment(sketch, "E101", {"start": v(15, -108) * mm, "end": v(15, -120) * mm});
            skArc(sketch, "E102", {"start": v(-15, -120) * mm, "mid": v(0, -135) * mm, "end": v(15, -120) * mm});
            skCircle(sketch, "E103", {"center": v(0, -120) * mm, "radius": 6 * mm});
            skLineSegment(sketch, "E104", {"start": v(0, -120) * mm, "end": v(0, -90) * mm, "construction": true});
            skLineSegment(sketch, "E105", {"start": v(-80, 0) * mm, "end": v(80, 0) * mm, "construction": true});
            skLineSegment(sketch, "E106.MirrorCS", {"start": v(15, 108) * mm, "end": v(15, 120) * mm});
            skLineSegment(sketch, "E107.MirrorCS", {"start": v(-15, 108) * mm, "end": v(-15, 120) * mm});
            skLineSegment(sketch, "E108.MirrorCS", {"start": v(0, 120) * mm, "end": v(0, 90) * mm, "construction": true});
            skLineSegment(sketch, "E109.MirrorCS", {"start": v(33, 90) * mm, "end": v(15, 108) * mm});
            skLineSegment(sketch, "E110.MirrorCS", {"start": v(-33, 90) * mm, "end": v(-15, 108) * mm});
            skCircle(sketch, "E111.MirrorC", {"center": v(0, 120) * mm, "radius": 6 * mm});
            skArc(sketch, "E112.MirrorCS", {"start": v(-15, 120) * mm, "mid": v(0, 135) * mm, "end": v(15, 120) * mm});
            skLineSegment(sketch, "E113.0", {"start": v(-70, -90) * mm, "end": v(70, -90) * mm});
            skSolve(sketch);
        }
        {
            var Q0;
            {var subQ1=sQuery(id+"F16.wireOp",EDGE,"E98");Q0=makeQuery(id+"F16.imprint","IMPRINT",FACE,{"disambiguationData":[TD([[makeQuery(id+"F16.imprint","IMPRINT",EDGE,{"derivedFrom":subQ1}),1.0]])]});}
            var Q1;
            Q1=makeQuery(id+"F16.imprint","IMPRINT",FACE,{"disambiguationData":[TD([[makeQuery(id+"F16.imprint","IMPRINT",EDGE,{"derivedFrom":sQuery(id+"F16.wireOp",EDGE,"E79.0")}),-1.0]])]});
            var Q2;
            Q2=makeQuery(id+"F16.imprint","IMPRINT",FACE,{"disambiguationData":[TD([[makeQuery(id+"F16.imprint","IMPRINT",EDGE,{"derivedFrom":sQuery(id+"F16.wireOp",EDGE,"E106.MirrorCS")}),1.0]])]});
            var Q3;
            Q3=makeQuery(id+"F2.opExtrude","CAP_FACE",FACE,{"disambiguationData":[OSD([sQuery(id+"F0.wireOp",EDGE,"E12"),sQuery(id+"F0.wireOp",EDGE,"E13"),sQuery(id+"F0.wireOp",EDGE,"E14"),sQuery(id+"F0.wireOp",EDGE,"E15"),sQuery(id+"F0.wireOp",EDGE,"E17.filletArc"),sQuery(id+"F0.wireOp",EDGE,"E18.filletArc"),sQuery(id+"F0.wireOp",EDGE,"E19.filletArc"),sQuery(id+"F0.wireOp",EDGE,"E20.filletArc"),sQuery(id+"F0.wireOp",EDGE,"E25.0"),sQuery(id+"F0.wireOp",EDGE,"E25.1"),sQuery(id+"F0.wireOp",EDGE,"E25.2"),sQuery(id+"F0.wireOp",EDGE,"E25.3"),sQuery(id+"F0.wireOp",EDGE,"E25.4"),sQuery(id+"F0.wireOp",EDGE,"E25.5"),sQuery(id+"F0.wireOp",EDGE,"E25.6"),sQuery(id+"F0.wireOp",EDGE,"E25.7")])],"isStart":false});
            extrude(context, id + "F17", {"entities" : qUnion([Q0, Q1, Q2]), "endBound" : BoundingType.UP_TO_SURFACE, "endBoundEntityFace" : qUnion([Q3]), "depth" : 25 * mm});
        }
    });
